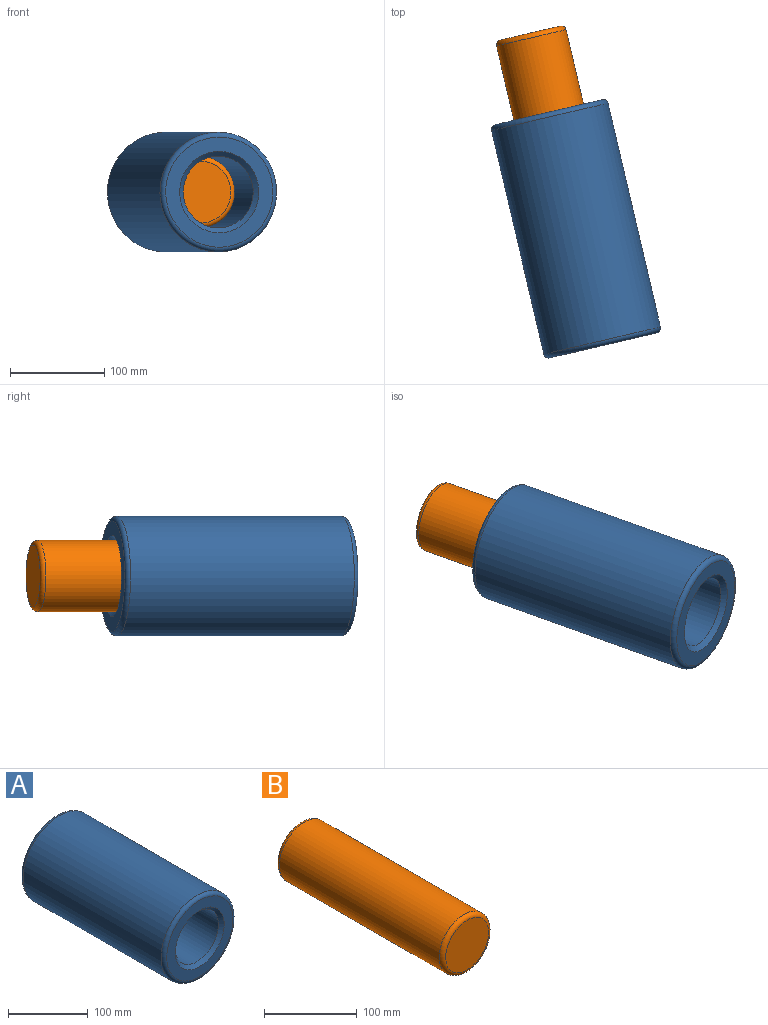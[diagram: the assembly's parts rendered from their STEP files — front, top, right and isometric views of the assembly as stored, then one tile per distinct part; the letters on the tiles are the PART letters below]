
ASSEMBLY  parts=2 mates=1
PART A: 8 faces, bbox 137.5x254x137.5 mm
  f0: cylinder r=38.1mm len=243.84mm, axis (0,1,0), area 58372.7mm2, adj f4,f5
  f1: cylinder r=63.5mm len=243.84mm, axis (0,1,0), area 97287.8mm2, adj f6,f7
  f2: plane 116.84x116.84mm, normal (0,-1,0), area 4864.4mm2, adj f4,f6
  f3: plane 116.84x116.84mm, normal (0,1,0), area 4864.4mm2, adj f5,f7
  f4: cone r=38.1mm half-angle=45deg, axis (0,-1,0), area 1834.5mm2, adj f0,f2
  f5: cone r=43.18mm half-angle=45deg, axis (0,1,0), area 1834.5mm2, adj f0,f3
  f6: torus R=58.42mm, axis (0,-1,0), area 3091.2mm2, adj f1,f2
  f7: torus R=58.42mm, axis (0,-1,0), area 3091.2mm2, adj f1,f3
PART B: 5 faces, bbox 81.9x254x81.9 mm
  f0: cylinder r=37.85mm len=243.84mm, axis (0,1,0), area 57983.6mm2, adj f3,f4
  f1: plane 65.53x65.53mm, normal (0,-1,0), area 3372.8mm2, adj f3
  f2: plane 65.53x65.53mm, normal (0,1,0), area 3372.8mm2, adj f4
  f3: torus R=32.77mm, axis (0,-1,0), area 1805mm2, adj f0,f1
  f4: torus R=32.77mm, axis (0,-1,0), area 1805mm2, adj f0,f2
PLACE A rot(axis=(0.99,0.11,0),180deg) t=(-45.79,-332.61,267.92)mm fixed
PLACE B rot(axis=(0,0,1),13.2deg) t=(-123.38,-1.34,267.92)mm
MATE slider B.f0 <-> A.f0  axis (0.23,-0.97,0) through (-65.46,-248.65,267.92)mm
